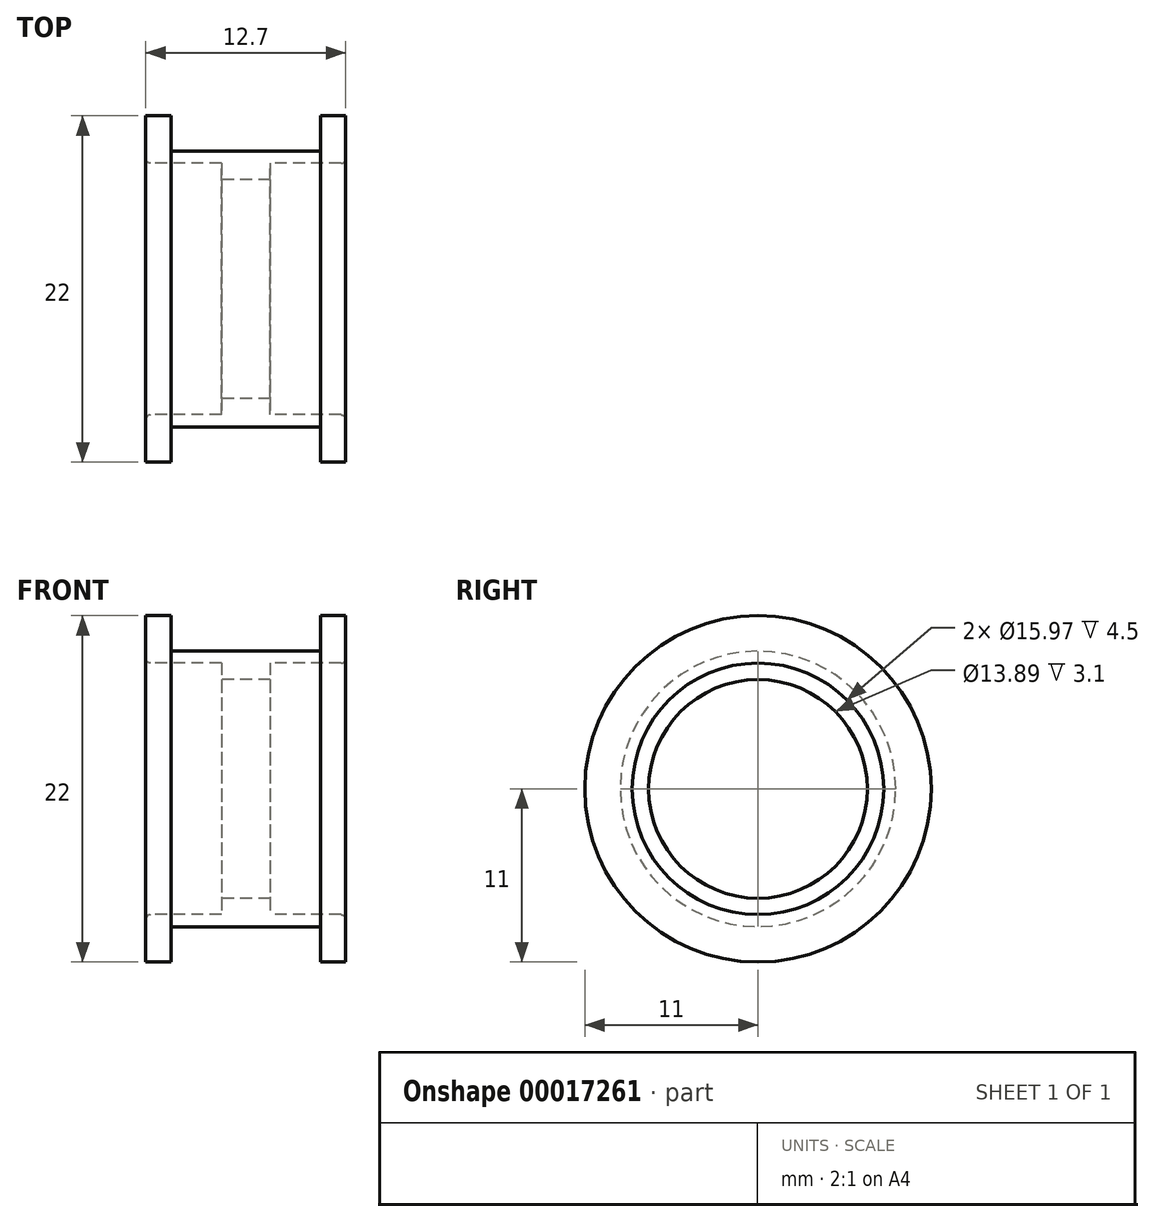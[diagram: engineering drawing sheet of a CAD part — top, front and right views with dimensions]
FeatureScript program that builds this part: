
annotation { "Feature Type Name" : "Feature", "Feature Type Description" : "" }
export const myFeature = defineFeature(function(context is Context, id is Id, definition is map)
    precondition{}
    {
        {
            var Q0;
            Q0=qCreatedBy(makeId("Front.planeOp"),FACE);
            var sketch = newSketch(context, id + "F0", { "sketchPlane" : qUnion([Q0])});
            skLineSegment(sketch, "E0", {"start": v(0, 11) * mm, "end": v(0, 7.99) * mm});
            skLineSegment(sketch, "E1", {"start": v(0, 7.99) * mm, "end": v(4.8, 7.99) * mm});
            skLineSegment(sketch, "E2", {"start": v(4.8, 7.99) * mm, "end": v(4.8, 6.95) * mm});
            skLineSegment(sketch, "E3", {"start": v(4.8, 6.95) * mm, "end": v(7.9, 6.95) * mm});
            skLineSegment(sketch, "E4", {"start": v(7.9, 6.94) * mm, "end": v(7.9, 7.99) * mm});
            skLineSegment(sketch, "E5", {"start": v(7.9, 7.99) * mm, "end": v(12.7, 7.99) * mm});
            skLineSegment(sketch, "E6", {"start": v(12.7, 7.99) * mm, "end": v(12.7, 11) * mm});
            skLineSegment(sketch, "E7", {"start": v(12.7, 11) * mm, "end": v(11.1, 11) * mm});
            skLineSegment(sketch, "E8", {"start": v(11.1, 11) * mm, "end": v(11.1, 8.75) * mm});
            skLineSegment(sketch, "E9", {"start": v(11.1, 8.75) * mm, "end": v(1.6, 8.75) * mm});
            skLineSegment(sketch, "E10", {"start": v(1.6, 8.75) * mm, "end": v(1.6, 11) * mm});
            skLineSegment(sketch, "E11", {"start": v(1.6, 11) * mm, "end": v(0, 11) * mm});
            skLineSegment(sketch, "E12", {"start": v(2.55, 0) * mm, "end": v(13, 0) * mm, "construction": true});
            skSolve(sketch);
        }
        {
            var Q0;
            Q0=makeQuery(id+"F0.imprint","IMPRINT",FACE,{"disambiguationData":[TD([[makeQuery(id+"F0.imprint","IMPRINT",EDGE,{"derivedFrom":sQuery(id+"F0.wireOp",EDGE,"E0")}),1.0]])]});
            var Q1;
            Q1=sQuery(id+"F0.wireOp",EDGE,"E12");
            revolve(context, id + "F1", {"entities" : qUnion([Q0]), "axis" : qUnion([Q1]), "revolveType" : RevolveType.FULL});
        }
        {
            var Q0;
            Q0=makeQuery(id+"F1.opRevolve","SWEPT_EDGE",EDGE,{"disambiguationData":[OSD([sQuery(id+"F0.wireOp",EDGE,"E0"),sQuery(id+"F0.wireOp",EDGE,"E1")])]});
            var Q1;
            Q1=makeQuery(id+"F1.opRevolve","SWEPT_EDGE",EDGE,{"disambiguationData":[OSD([sQuery(id+"F0.wireOp",EDGE,"E5"),sQuery(id+"F0.wireOp",EDGE,"E6")])]});
            fillet(context, id + "F2", {"entities" : qUnion([Q0, Q1]), "radius" : 0.3 * mm, "allowEdgeOverflow" : false});
        }
    });
